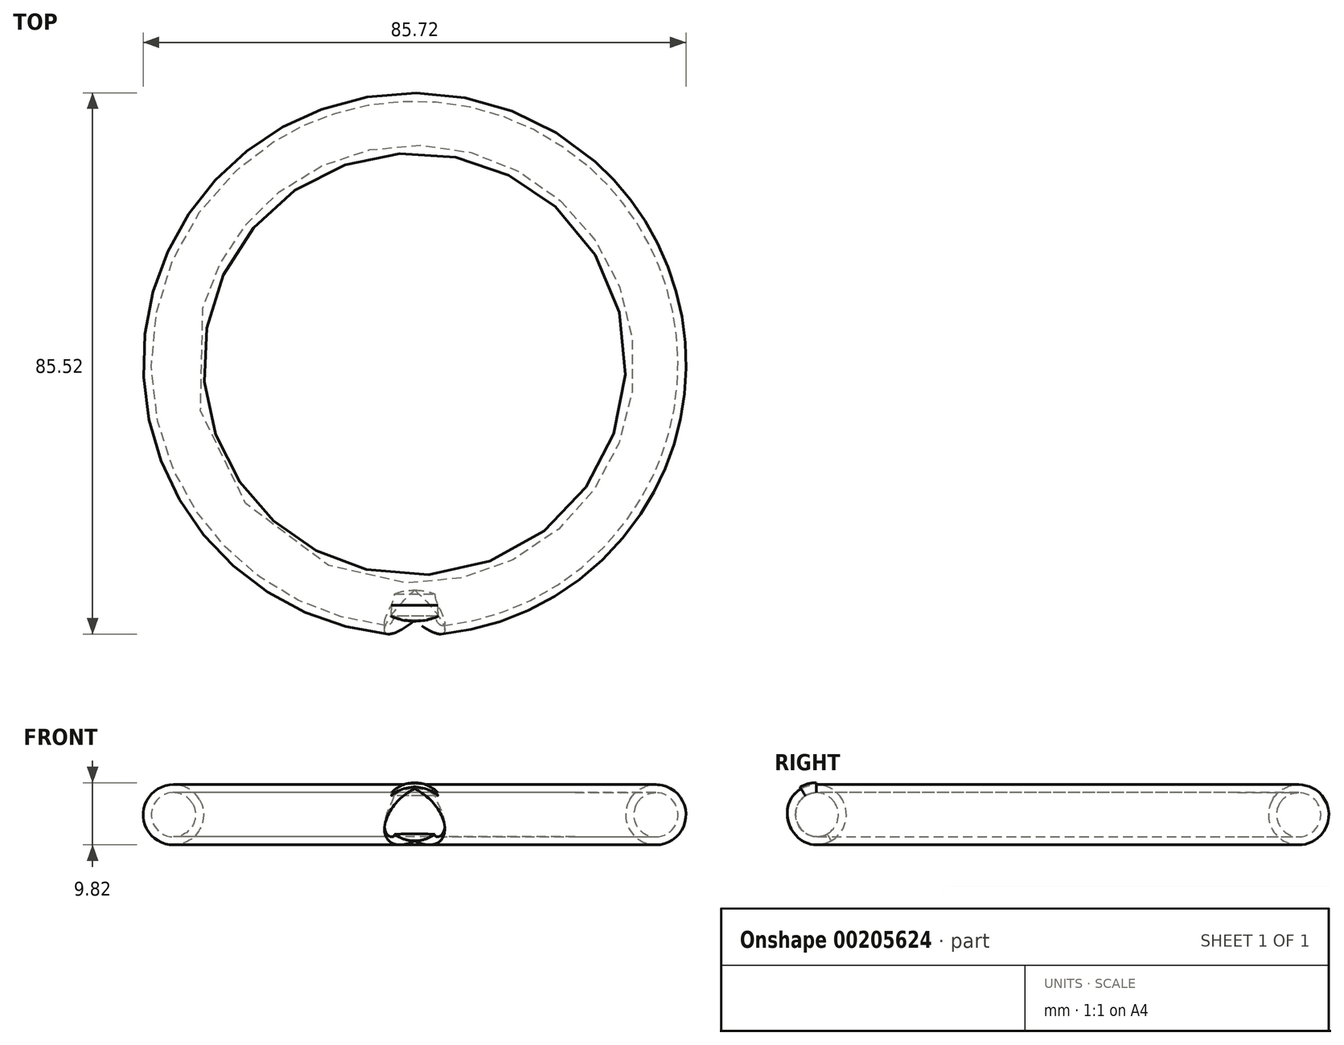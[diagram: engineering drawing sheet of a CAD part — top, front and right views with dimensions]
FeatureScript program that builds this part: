
annotation { "Feature Type Name" : "Feature", "Feature Type Description" : "" }
export const myFeature = defineFeature(function(context is Context, id is Id, definition is map)
    precondition{}
    {
        {
            var Q0;
            Q0=qCreatedBy(makeId("Front.planeOp"),FACE);
            var sketch = newSketch(context, id + "F0", { "sketchPlane" : qUnion([Q0])});
            skLineSegment(sketch, "E0", {"start": v(0, 0) * mm, "end": v(-38.1, 0) * mm, "construction": true});
            skCircle(sketch, "E1", {"center": v(-38.1, 0) * mm, "radius": 3.5 * mm});
            skCircle(sketch, "E2", {"center": v(-38.1, 0) * mm, "radius": 4.76 * mm});
            skLineSegment(sketch, "E3", {"start": v(0, 0) * mm, "end": v(0, 11.57) * mm, "construction": true});
            skSolve(sketch);
        }
        {
            var Q0;
            Q0=makeQuery(id+"F0.imprint","IMPRINT",FACE,{"disambiguationData":[TD([[makeQuery(id+"F0.imprint","IMPRINT",EDGE,{"derivedFrom":sQuery(id+"F0.wireOp",EDGE,"E1")}),-1.0]])]});
            var Q1;
            Q1=sQuery(id+"F0.wireOp",EDGE,"E3");
            revolve(context, id + "F1", {"entities" : qUnion([Q0]), "axis" : qUnion([Q1]), "revolveType" : RevolveType.FULL});
        }
        {
            var Q0;
            Q0=qCreatedBy(makeId("Front.planeOp"),FACE);
            cPlane(context, id + "F2", {"entities" : qUnion([Q0]), "cplaneType" : CPlaneType.OFFSET, "offset" : 38.1 * mm, "width" : 152.4 * mm, "height" : 152.4 * mm});
        }
        {
            var Q0;
            Q0=qCreatedBy(id+"F2.planeOp",FACE);
            var sketch = newSketch(context, id + "F3", { "sketchPlane" : qUnion([Q0])});
            skArc(sketch, "E4", {"start": v(5.06, 0) * mm, "mid": v(0, 5.06) * mm, "end": v(-5.06, 0) * mm});
            skLineSegment(sketch, "E5", {"start": v(-5.06, 0) * mm, "end": v(5.06, 0) * mm});
            skSolve(sketch);
        }
        {
            var Q0;
            Q0 = qSketchRegion(id + "F3", true);
            var Q1;
            Q1=sQuery(id+"F3.wireOp",EDGE,"E5");
            revolve(context, id + "F4", {"entities" : qUnion([Q0]), "axis" : qUnion([Q1]), "revolveType" : RevolveType.ONE_DIRECTION, "angle" : 30 * degree});
        }
        {
            var Q0;
            Q0=makeQuery(id+"F4.opRevolve","CAP_FACE",FACE,{"disambiguationData":[OSD([sQuery(id+"F3.wireOp",EDGE,"E4"),sQuery(id+"F3.wireOp",EDGE,"E5")])],"isStart":false});
            var sketch = newSketch(context, id + "F5", { "sketchPlane" : qUnion([Q0])});
            skCircle(sketch, "E6", {"center": v(0, 19.05) * mm, "radius": 3.5 * mm});
            skCircle(sketch, "E7", {"center": v(0, 19.05) * mm, "radius": 4.76 * mm});
            skSolve(sketch);
        }
        {
            var Q0;
            Q0 = qSketchRegion(id + "F5", true);
            extrude(context, id + "F6", {"entities" : qUnion([Q0]), "offsetDistance" : 25.4 * mm, "depth" : 25.4 * mm});
        }
        {
            var Q0;
            {var subQ0=sQuery(id+"F5.wireOp",EDGE,"E6");var subQ1=makeQuery(id+"F4.opRevolve","CAP_EDGE",EDGE,{"disambiguationData":[OSD([sQuery(id+"F3.wireOp",EDGE,"E5")])],"isStart":true});var subQ2=makeQuery(id+"F5.imprint","INTERSECT",VERTEX,{"disambiguationData":[OD(0.0)],"derivedFrom":[subQ1,subQ0]});Q0=makeQuery(id+"F5.imprint","IMPRINT",FACE,{"disambiguationData":[TD([[makeQuery(id+"F5.imprint","IMPRINT",EDGE,{"disambiguationData":[TD([[subQ2,1.0]])],"derivedFrom":subQ0}),1.0]])]});}
            var Q1;
            {var subQ0=sQuery(id+"F5.wireOp",EDGE,"E6");var subQ1=makeQuery(id+"F4.opRevolve","CAP_EDGE",EDGE,{"disambiguationData":[OSD([sQuery(id+"F3.wireOp",EDGE,"E5")])],"isStart":true});var subQ2=makeQuery(id+"F5.imprint","INTERSECT",VERTEX,{"disambiguationData":[OD(0.0)],"derivedFrom":[subQ1,subQ0]});Q1=makeQuery(id+"F5.imprint","IMPRINT",FACE,{"disambiguationData":[TD([[makeQuery(id+"F5.imprint","IMPRINT",EDGE,{"disambiguationData":[TD([[subQ2,-1.0]])],"derivedFrom":subQ0}),1.0]])]});}
            var Q2;
            {var subQ0=sQuery(id+"F5.wireOp",EDGE,"E6");var subQ1=makeQuery(id+"F4.opRevolve","CAP_EDGE",EDGE,{"disambiguationData":[OSD([sQuery(id+"F3.wireOp",EDGE,"E5")])],"isStart":true});var subQ2=makeQuery(id+"F5.imprint","INTERSECT",VERTEX,{"disambiguationData":[OD(0.0)],"derivedFrom":[subQ1,subQ0]});Q2=makeQuery(id+"F5.imprint","IMPRINT",FACE,{"disambiguationData":[TD([[makeQuery(id+"F5.imprint","IMPRINT",EDGE,{"disambiguationData":[TD([[subQ2,-1.0]])],"derivedFrom":subQ0}),-1.0]])]});}
            var Q3;
            {var subQ0=sQuery(id+"F5.wireOp",EDGE,"E6");var subQ1=makeQuery(id+"F4.opRevolve","CAP_EDGE",EDGE,{"disambiguationData":[OSD([sQuery(id+"F3.wireOp",EDGE,"E5")])],"isStart":true});var subQ2=makeQuery(id+"F5.imprint","INTERSECT",VERTEX,{"disambiguationData":[OD(0.0)],"derivedFrom":[subQ1,subQ0]});Q3=makeQuery(id+"F5.imprint","IMPRINT",FACE,{"disambiguationData":[TD([[makeQuery(id+"F5.imprint","IMPRINT",EDGE,{"disambiguationData":[TD([[subQ2,1.0]])],"derivedFrom":subQ0}),-1.0]])]});}
            extrude(context, id + "F7", {"entities" : qUnion([Q0, Q1, Q2, Q3]), "operationType" : NewBodyOperationType.REMOVE, "depth" : 25.4 * mm});
        }
        {
            var Q0;
            Q0=makeQuery(id+"F0.imprint","IMPRINT",FACE,{"disambiguationData":[TD([[makeQuery(id+"F0.imprint","IMPRINT",EDGE,{"derivedFrom":sQuery(id+"F0.wireOp",EDGE,"E1")}),1.0]])]});
            var Q1;
            Q1=sQuery(id+"F0.wireOp",EDGE,"E3");
            revolve(context, id + "F8", {"operationType" : NewBodyOperationType.REMOVE, "entities" : qUnion([Q0]), "axis" : qUnion([Q1]), "revolveType" : RevolveType.FULL, "oppositeDirection" : true});
        }
    });
